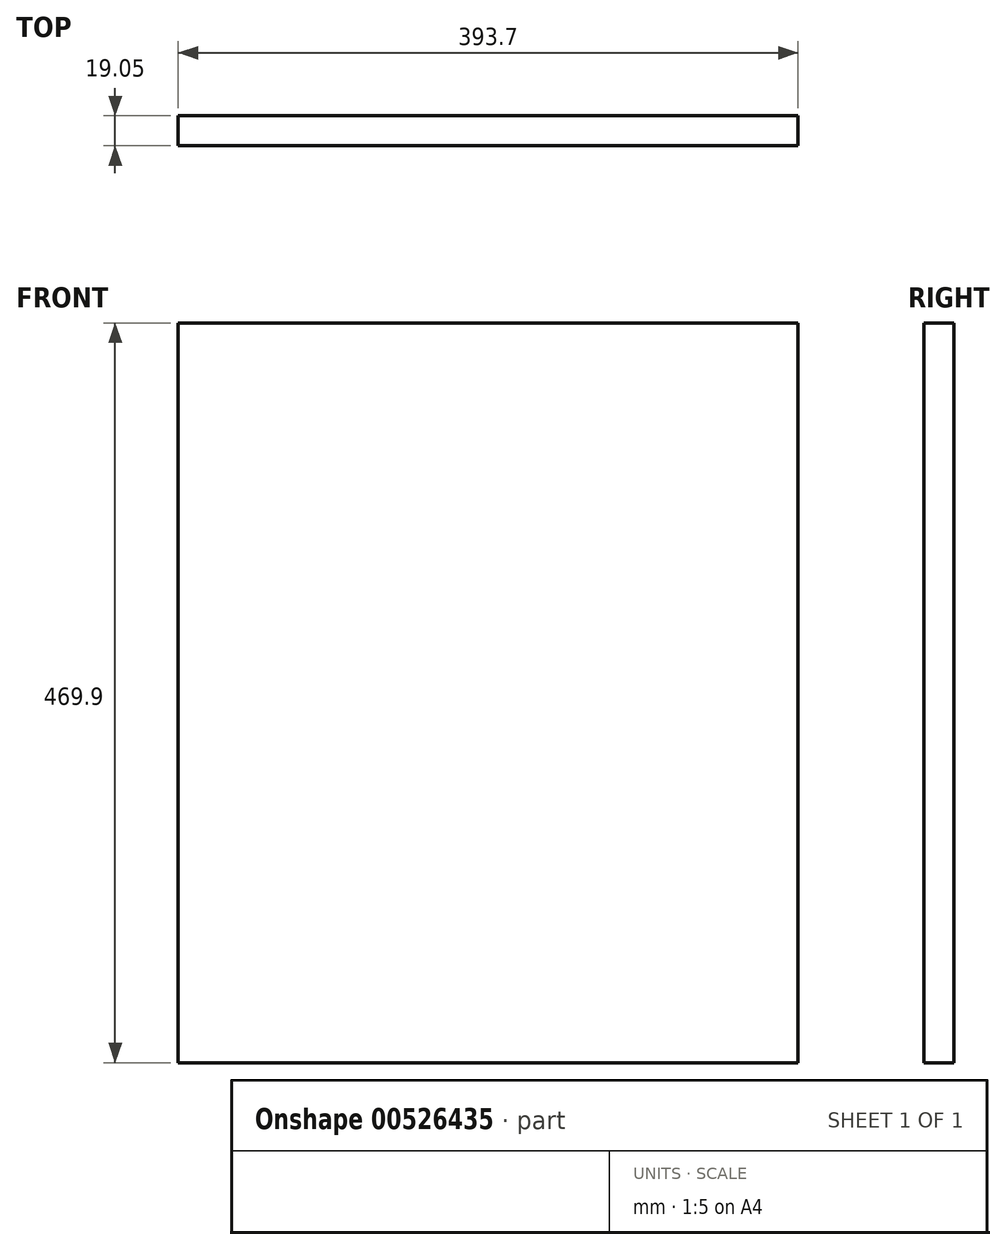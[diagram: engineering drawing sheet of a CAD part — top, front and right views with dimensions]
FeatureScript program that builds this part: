
annotation { "Feature Type Name" : "Feature", "Feature Type Description" : "" }
export const myFeature = defineFeature(function(context is Context, id is Id, definition is map)
    precondition{}
    {
        {
            var Q0;
            Q0=qCreatedBy(makeId("Front.planeOp"),FACE);
            var sketch = newSketch(context, id + "F0", { "sketchPlane" : qUnion([Q0])});
            skLineSegment(sketch, "E0.bottom", {"start": v(196.85, 234.95) * mm, "end": v(-196.85, 234.95) * mm});
            skLineSegment(sketch, "E0.top", {"start": v(196.85, -234.95) * mm, "end": v(-196.85, -234.95) * mm});
            skLineSegment(sketch, "E0.left", {"start": v(196.85, 234.95) * mm, "end": v(196.85, -234.95) * mm});
            skLineSegment(sketch, "E0.right", {"start": v(-196.85, 234.95) * mm, "end": v(-196.85, -234.95) * mm});
            skPoint(sketch, "E0.middle", {"position": v(0, 0) * mm});
            skSolve(sketch);
        }
        {
            var Q0;
            Q0=makeQuery(id+"F0.imprint","IMPRINT",FACE,{"disambiguationData":[TD([[makeQuery(id+"F0.imprint","IMPRINT",EDGE,{"derivedFrom":sQuery(id+"F0.wireOp",EDGE,"E0.bottom")}),1.0]])]});
            extrude(context, id + "F1", {"entities" : qUnion([Q0]), "depth" : 19.05 * mm, "offsetDistance" : 25.4 * mm});
        }
    });
